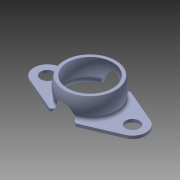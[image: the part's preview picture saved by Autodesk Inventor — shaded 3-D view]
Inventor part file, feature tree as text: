
AUTODESK INVENTOR PART (.ipt)
format: ipt  version: 2016 SP1 (Build 200210100, 210)  size: 273,920 bytes
history: native  units: in
note: dims shown in document units (in); Inventor stores cm internally (conversion verified against a paired STEP export)
features: extrude x1
ambient origin geometry x8: Origin, YZ Plane, XZ Plane, XY Plane, X Axis, Y Axis, Z Axis, Center Point
bodies: Solid1 (feature_tree)
feature tree (1):
  extrude  "Extrude5"  [1 undecoded]
note: 1 required parameter value undecoded (feature->parameter linkage not recoverable at this tier; creation-order binding heuristic only, values carry confidence <= 0.55)
